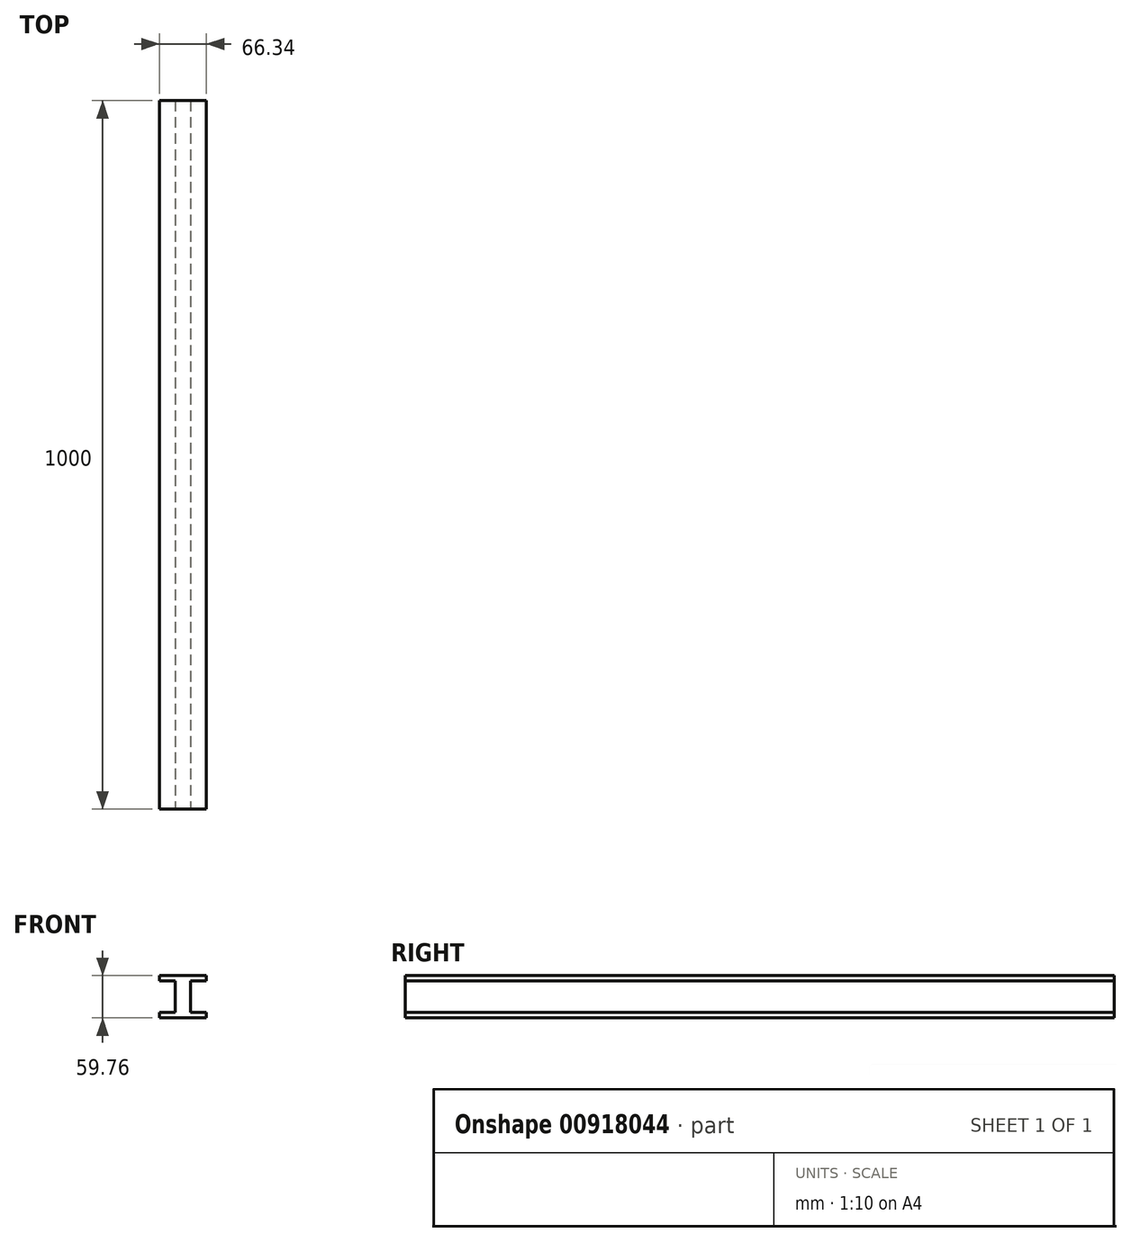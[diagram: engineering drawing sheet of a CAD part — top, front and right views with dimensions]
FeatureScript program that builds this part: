
annotation { "Feature Type Name" : "Feature", "Feature Type Description" : "" }
export const myFeature = defineFeature(function(context is Context, id is Id, definition is map)
    precondition{}
    {
        {
            var Q0;
            Q0=qCreatedBy(makeId("Front.planeOp"),FACE);
            var sketch = newSketch(context, id + "F0", { "sketchPlane" : qUnion([Q0])});
            skLineSegment(sketch, "E0", {"start": v(-10.85, 0) * mm, "end": v(-10.85, 22.14) * mm});
            skLineSegment(sketch, "E1", {"start": v(-10.85, 22.14) * mm, "end": v(-33.17, 22.14) * mm});
            skLineSegment(sketch, "E2", {"start": v(-33.17, 29.88) * mm, "end": v(-33.17, 22.14) * mm});
            skLineSegment(sketch, "E3", {"start": v(0, 29.88) * mm, "end": v(-33.17, 29.88) * mm});
            skLineSegment(sketch, "E4", {"start": v(0, 32.88) * mm, "end": v(0, -13.7) * mm});
            skLineSegment(sketch, "E5", {"start": v(-33.53, 0) * mm, "end": v(30.77, 0) * mm});
            skLineSegment(sketch, "E6.MirrorCS", {"start": v(0, 29.88) * mm, "end": v(33.17, 29.88) * mm});
            skLineSegment(sketch, "E7.MirrorCS", {"start": v(10.85, 22.14) * mm, "end": v(33.17, 22.14) * mm});
            skLineSegment(sketch, "E8.MirrorCS", {"start": v(33.17, 29.88) * mm, "end": v(33.17, 22.14) * mm});
            skLineSegment(sketch, "E9.MirrorCS", {"start": v(10.85, 0) * mm, "end": v(10.85, 22.14) * mm});
            skLineSegment(sketch, "E10.MirrorCS", {"start": v(10.85, 0) * mm, "end": v(10.85, -22.14) * mm});
            skLineSegment(sketch, "E11.MirrorCS", {"start": v(10.85, -22.14) * mm, "end": v(33.17, -22.14) * mm});
            skLineSegment(sketch, "E12.MirrorCS", {"start": v(33.17, -29.88) * mm, "end": v(33.17, -22.14) * mm});
            skLineSegment(sketch, "E13.MirrorCS", {"start": v(0, -29.88) * mm, "end": v(33.17, -29.88) * mm});
            skLineSegment(sketch, "E14.MirrorCS", {"start": v(-33.17, -29.88) * mm, "end": v(-33.17, -22.14) * mm});
            skLineSegment(sketch, "E15.MirrorCS", {"start": v(-10.85, -22.14) * mm, "end": v(-33.17, -22.14) * mm});
            skLineSegment(sketch, "E16.MirrorCS", {"start": v(-10.85, 0) * mm, "end": v(-10.85, -22.14) * mm});
            skLineSegment(sketch, "E17.MirrorCS", {"start": v(0, -29.88) * mm, "end": v(-33.17, -29.88) * mm});
            skSolve(sketch);
        }
        {
            var Q0;
            {var subQ0=sQuery(id+"F0.wireOp",EDGE,"E6.MirrorCS");Q0=makeQuery(id+"F0.imprint","IMPRINT",FACE,{"disambiguationData":[TD([[makeQuery(id+"F0.imprint","IMPRINT",EDGE,{"derivedFrom":subQ0}),-1.0]])]});}
            var Q1;
            {var subQ0=sQuery(id+"F0.wireOp",EDGE,"E10.MirrorCS");Q1=makeQuery(id+"F0.imprint","IMPRINT",FACE,{"disambiguationData":[TD([[makeQuery(id+"F0.imprint","IMPRINT",EDGE,{"derivedFrom":subQ0}),-1.0]])]});}
            var Q2;
            {var subQ1=sQuery(id+"F0.wireOp",EDGE,"E0");Q2=makeQuery(id+"F0.imprint","IMPRINT",FACE,{"disambiguationData":[TD([[makeQuery(id+"F0.imprint","IMPRINT",EDGE,{"derivedFrom":subQ1}),-1.0]])]});}
            extrude(context, id + "F1", {"entities" : qUnion([Q0, Q1, Q2]), "oppositeDirection" : true, "depth" : 1000 * mm, "offsetDistance" : 25 * mm});
        }
    });
